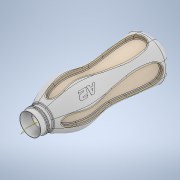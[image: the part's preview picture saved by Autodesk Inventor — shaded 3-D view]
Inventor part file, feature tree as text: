
AUTODESK INVENTOR PART (.ipt)
format: ipt  version: 2021 (Build 250183000, 183)  size: 10,852,352 bytes
history: native  units: mm
features: sketch x13, plane x11, other x6, fillet x5, thicken_offset x4, surface_op x4, extrude x2, loft x1, pattern_circular x1, shell x1, sweep x1, emboss x1
ambient origin geometry x8: Origin, YZ Plane, XZ Plane, XY Plane, X Axis, Y Axis, Z Axis, Center Point
bodies: Solid1 (feature_tree), Solid2 (feature_tree)
feature tree (50):
  sketch  "Sketch1"  dims[d0=80.0mm d1=80.0mm d2=25.0mm]
  plane  "Work Plane1"
  sketch  "Sketch2"  dims[d3=25.0mm d4=25.0mm d5=25.0mm]
  plane  "Work Plane2"
  sketch  "Sketch4"  dims[d6=35.0mm d7=85.0mm d8=80.0mm]
  plane  "Work Plane3"
  sketch  "Sketch5"  dims[d9=75.0mm]
  plane  "Work Plane4"
  sketch  "Sketch6"  dims[d10=65.0mm d11=90.0mm d12=45.0mm d13=55.0mm d14=5.0mm]
  plane  "Work Plane5"
  loft  "Loft1"
  fillet  "Fillet1"  Radius=25.0mm
  extrude  "Extrusion1"  Depth=25.0mm
  fillet  "Fillet2"  Radius=25.0mm
  extrude  "Extrusion2"  Depth=85.0mm
  fillet  "Fillet3"  Radius=80.0mm
  plane  "Work Plane6"
  sketch  "Sketch13"  dims[d20=0.0mm d21=90.0deg]
  pattern_circular  "Circular Pattern1"  Count=9  [1 undecoded]
  thicken_offset  "Thicken1"
  thicken_offset  "Thicken2"
  thicken_offset  "Thicken3"
  thicken_offset  "Thicken4"
  fillet  "Fillet4"  Radius=45.0mm
  fillet  "Fillet5"  Radius=55.0mm
  shell  "Shell1"  Thickness=5.0mm
  plane  "Work Plane7"
  sketch  "Sketch14"  dims[d22=0.0mm d23=90.0deg]
  sketch  "3D Sketch2"
  plane  "Work Plane10"
  sweep  "Sweep1"
  plane  "Work Plane14"
  emboss  "Emboss1"
  sketch  "Sketch7"  dims[d15=50.0mm d16=0.0mm d17=90.0deg]
  sketch  "Sketch12"  dims[d18=0.0mm d19=90.0deg]
  sketch  "3D Sketch1"
  other  "Project to Surface1"
  other  "Srf1"
  other  "Srf2"
  other  "Srf3"
  other  "Srf4"
  other  "Helical Curve1"
  sketch  "Sketch17"  dims[d24=0.0mm d25=90.0deg]
  plane  "Work Plane12"
  plane  "Work Plane13"
  sketch  "Sketch19"  dims[d26=0.0mm d27=90.0deg d28=10.0mm d31=5.0mm d32=0.0mm d33=2.5mm d34=45.0mm d35=25.0mm d36=0.0mm d37=2.0mm d38=87.75mm d39=160.0mm d40=15.0mm d42=40.0mm d43=22.0mm d44=11.0mm d47=180.0mm d48=500.0mm d49=22.0mm d50=0.0mm d51=40.0mm d52=360.0deg d54=15.0mm d55=15.0mm d56=15.0mm d57=15.0mm d58=15.0mm d59=15.0mm d60=15.0mm d61=15.0mm d62=1.5mm d63=1.5mm d64=1.0mm d65=-10.0mm d66=8.0mm d67=20.0mm d68=45.0mm d69=0.0mm d72=-10.0mm d74=0.0mm d75=0.0mm d76=45.0deg d77=-123.75mm d78=846.0mm d79=0.25mm d80=0.0mm]
  surface_op  "Boundary Patch1"
  surface_op  "Boundary Patch2"
  surface_op  "Boundary Patch3"
  surface_op  "Boundary Patch4"
note: 1 required parameter value undecoded (feature->parameter linkage not recoverable at this tier; creation-order binding heuristic only, values carry confidence <= 0.55)
